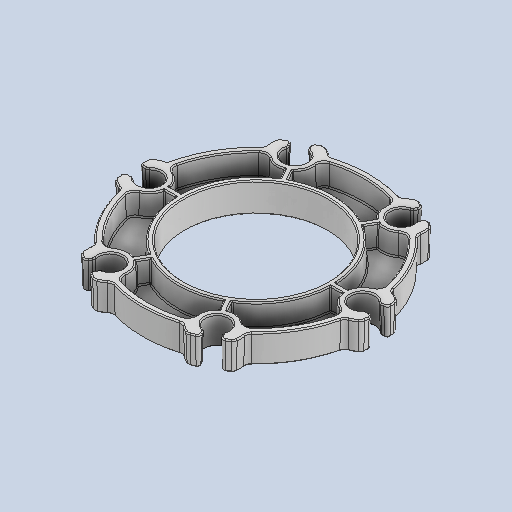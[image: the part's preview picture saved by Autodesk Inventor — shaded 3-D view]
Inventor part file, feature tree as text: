
AUTODESK INVENTOR PART (.ipt)
format: ipt  version: 2023 (Build 270158000, 158)  size: 875,520 bytes
history: native  units: in
note: dims shown in document units (in); Inventor stores cm internally (conversion verified against a paired STEP export)
features: fillet x1
ambient origin geometry x8: Origin, YZ Plane, XZ Plane, XY Plane, X Axis, Y Axis, Z Axis, Center Point
bodies: Solid1 (feature_tree)
feature tree (1):
  fillet  "Fillet3"  [1 undecoded]
note: 1 required parameter value undecoded (feature->parameter linkage not recoverable at this tier; creation-order binding heuristic only, values carry confidence <= 0.55)
